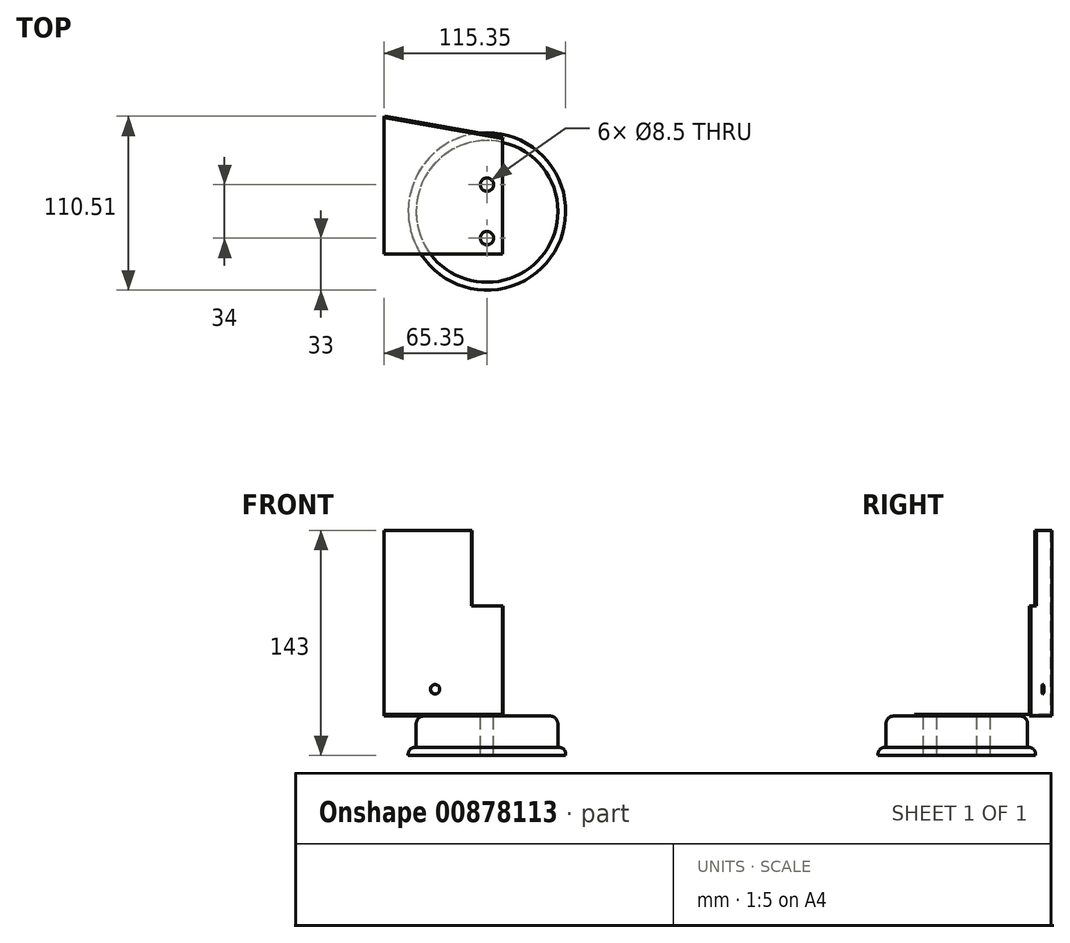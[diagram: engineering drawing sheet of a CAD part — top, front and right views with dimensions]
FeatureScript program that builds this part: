
annotation { "Feature Type Name" : "Feature", "Feature Type Description" : "" }
export const myFeature = defineFeature(function(context is Context, id is Id, definition is map)
    precondition{}
    {
        {
            var Q0;
            Q0=qCreatedBy(makeId("Top.planeOp"),FACE);
            var sketch = newSketch(context, id + "F0", { "sketchPlane" : qUnion([Q0])});
            skCircle(sketch, "E0", {"center": v(0, 0) * mm, "radius": 45 * mm});
            skLineSegment(sketch, "E1", {"start": v(0, 0) * mm, "end": v(0, 17) * mm, "construction": true});
            skLineSegment(sketch, "E2", {"start": v(0, 0) * mm, "end": v(0, -17) * mm, "construction": true});
            skCircle(sketch, "E3", {"center": v(0, 17) * mm, "radius": 4.25 * mm});
            skCircle(sketch, "E4", {"center": v(0, -17) * mm, "radius": 4.25 * mm});
            skLineSegment(sketch, "E5", {"start": v(0, -8.5) * mm, "end": v(10, -8.5) * mm, "construction": true});
            skLineSegment(sketch, "E6", {"start": v(0, -17) * mm, "end": v(0, -27) * mm, "construction": true});
            skLineSegment(sketch, "E7", {"start": v(0, 17) * mm, "end": v(0, 48) * mm, "construction": true});
            skLineSegment(sketch, "E8", {"start": v(0, 48) * mm, "end": v(-33, 48) * mm, "construction": true});
            skLineSegment(sketch, "E9", {"start": v(-33, 48) * mm, "end": v(-33, 73.27) * mm, "construction": true});
            skLineSegment(sketch, "E10", {"start": v(-68.94, 60.16) * mm, "end": v(-68.94, -27) * mm});
            skLineSegment(sketch, "E11", {"start": v(-68.94, -27) * mm, "end": v(10, -27) * mm});
            skLineSegment(sketch, "E12", {"start": v(10, -27) * mm, "end": v(10, 46.24) * mm});
            skLineSegment(sketch, "E13", {"start": v(10, 46.24) * mm, "end": v(-68.94, 60.16) * mm});
            skPoint(sketch, "E14", {"position": v(-33, 53.82) * mm});
            skSolve(sketch);
        }
        {
            var Q0;
            Q0=makeQuery(id+"F0.imprint","IMPRINT",FACE,{"disambiguationData":[TD([[makeQuery(id+"F0.imprint","IMPRINT",EDGE,{"derivedFrom":sQuery(id+"F0.wireOp",EDGE,"E0")}),1.0]])]});
            var Q1;
            Q1=makeQuery(id+"F0.imprint","IMPRINT",FACE,{"disambiguationData":[TD([[makeQuery(id+"F0.imprint","IMPRINT",EDGE,{"derivedFrom":sQuery(id+"F0.wireOp",EDGE,"E3")}),-1.0]])]});
            extrude(context, id + "F1", {"entities" : qUnion([Q0, Q1]), "oppositeDirection" : true, "depth" : 20 * mm, "offsetDistance" : 25 * mm});
        }
        {
            var Q0;
            Q0=makeQuery(id+"F1.opExtrude","CAP_EDGE",EDGE,{"disambiguationData":[OSD([sQuery(id+"F0.wireOp",EDGE,"E0")])],"isStart":true});
            fillet(context, id + "F2", {"entities" : qUnion([Q0]), "radius" : 5 * mm, "tangentPropagation" : true, "allowEdgeOverflow" : false});
        }
        {
            var Q0;
            Q0=makeQuery(id+"F1.opExtrude","CAP_FACE",FACE,{"disambiguationData":[OSD([sQuery(id+"F0.wireOp",EDGE,"E0")])],"isStart":false});
            var sketch = newSketch(context, id + "F3", { "sketchPlane" : qUnion([Q0])});
            skCircle(sketch, "E15", {"center": v(0, 0) * mm, "radius": 50 * mm});
            skSolve(sketch);
        }
        {
            var Q0;
            Q0=makeQuery(id+"F3.imprint","IMPRINT",FACE,{"disambiguationData":[TD([[makeQuery(id+"F3.imprint","IMPRINT",EDGE,{"derivedFrom":sQuery(id+"F3.wireOp",EDGE,"E15")}),1.0]])]});
            var Q1;
            Q1=makeQuery(id+"F3.imprint","IMPRINT",FACE,{"disambiguationData":[TD([[makeQuery(id+"F3.imprint","IMPRINT",EDGE,{"derivedFrom":makeQuery(id+"F1.opExtrude","CAP_EDGE",EDGE,{"disambiguationData":[OSD([sQuery(id+"F0.wireOp",EDGE,"E0")])],"isStart":false})}),-1.0]])]});
            extrude(context, id + "F4", {"entities" : qUnion([Q0, Q1]), "depth" : 5 * mm, "offsetDistance" : 25 * mm});
        }
        {
            var Q0;
            Q0=makeQuery(id+"F4.opExtrude","CAP_EDGE",EDGE,{"disambiguationData":[OSD([sQuery(id+"F3.wireOp",EDGE,"E15")])],"isStart":true});
            fillet(context, id + "F5", {"entities" : qUnion([Q0]), "radius" : 4 * mm, "tangentPropagation" : true, "allowEdgeOverflow" : false});
        }
        {
            var Q0;
            Q0=makeQuery(id+"F1.opExtrude","CAP_FACE",FACE,{"disambiguationData":[OSD([sQuery(id+"F0.wireOp",EDGE,"E0"),sQuery(id+"F0.wireOp",EDGE,"E11"),sQuery(id+"F0.wireOp",EDGE,"E12")])],"isStart":true});
            var sketch = newSketch(context, id + "F6", { "sketchPlane" : qUnion([Q0])});
            skLineSegment(sketch, "E16", {"start": v(0, 0) * mm, "end": v(0, 17) * mm, "construction": true});
            skLineSegment(sketch, "E17", {"start": v(0, 0) * mm, "end": v(0, -17) * mm, "construction": true});
            skCircle(sketch, "E18", {"center": v(0, 17) * mm, "radius": 4.25 * mm});
            skCircle(sketch, "E19", {"center": v(0, -17) * mm, "radius": 4.25 * mm});
            skLineSegment(sketch, "E20", {"start": v(0, 17) * mm, "end": v(0, 48) * mm, "construction": true});
            skLineSegment(sketch, "E21", {"start": v(0, 48) * mm, "end": v(-33, 48) * mm, "construction": true});
            skLineSegment(sketch, "E22", {"start": v(-33, 48) * mm, "end": v(-33, 83.41) * mm, "construction": true});
            skLineSegment(sketch, "E23", {"start": v(-65.35, 59.52) * mm, "end": v(-65.35, -27) * mm});
            skLineSegment(sketch, "E24", {"start": v(-65.35, -27) * mm, "end": v(10, -27) * mm});
            skLineSegment(sketch, "E25", {"start": v(10, -27) * mm, "end": v(10, 46.24) * mm});
            skLineSegment(sketch, "E26", {"start": v(10, 46.24) * mm, "end": v(-65.35, 59.52) * mm});
            skLineSegment(sketch, "E27", {"start": v(10, -17) * mm, "end": v(0, -17) * mm, "construction": true});
            skLineSegment(sketch, "E28", {"start": v(0, -17) * mm, "end": v(0, -27) * mm, "construction": true});
            skSolve(sketch);
        }
        {
            var Q0;
            {var subQ6=sQuery(id+"F6.wireOp",EDGE,"E23");Q0=makeQuery(id+"F6.imprint","IMPRINT",FACE,{"disambiguationData":[TD([[makeQuery(id+"F6.imprint","IMPRINT",EDGE,{"derivedFrom":subQ6}),1.0]])]});}
            var Q1;
            Q1=makeQuery(id+"F6.imprint","IMPRINT",FACE,{"disambiguationData":[TD([[makeQuery(id+"F6.imprint","IMPRINT",EDGE,{"derivedFrom":sQuery(id+"F6.wireOp",EDGE,"E18")}),-1.0]])]});
            extrude(context, id + "F7", {"entities" : qUnion([Q0, Q1]), "depth" : 1 * mm, "offsetDistance" : 25 * mm});
        }
        {
            var Q0;
            Q0=makeQuery(id+"F7.opExtrude","SWEPT_FACE",FACE,{"disambiguationData":[OSD([sQuery(id+"F6.wireOp",EDGE,"E26")])]});
            var sketch = newSketch(context, id + "F8", { "sketchPlane" : qUnion([Q0])});
            skLineSegment(sketch, "E29.bottom", {"start": v(-1.82, 0) * mm, "end": v(74.7, 0) * mm});
            skLineSegment(sketch, "E29.right", {"start": v(74.7, 0) * mm, "end": v(74.7, 118) * mm});
            skPoint(sketch, "E30", {"position": v(41.84, 0) * mm});
            skLineSegment(sketch, "E31", {"start": v(41.84, 0) * mm, "end": v(41.84, 17) * mm, "construction": true});
            skCircle(sketch, "E32", {"center": v(41.84, 17) * mm, "radius": 3 * mm});
            skLineSegment(sketch, "E33", {"start": v(18.18, 0) * mm, "end": v(18.18, 70) * mm, "construction": true});
            skLineSegment(sketch, "E34", {"start": v(18.18, 70) * mm, "end": v(-1.82, 70) * mm, "construction": true});
            skLineSegment(sketch, "E35", {"start": v(18.18, 70) * mm, "end": v(18.18, 118) * mm});
            skLineSegment(sketch, "E36", {"start": v(18.18, 118) * mm, "end": v(74.7, 118) * mm});
            skLineSegment(sketch, "E37", {"start": v(18.18, 70) * mm, "end": v(-1.82, 70) * mm});
            skLineSegment(sketch, "E38", {"start": v(-1.82, 70) * mm, "end": v(-1.82, 0) * mm});
            skSolve(sketch);
        }
        {
            var Q0;
            {var subQ0=sQuery(id+"F8.wireOp",EDGE,"E29.bottom");Q0=makeQuery(id+"F8.imprint","IMPRINT",FACE,{"disambiguationData":[TD([[makeQuery(id+"F8.imprint","IMPRINT",EDGE,{"derivedFrom":subQ0}),1.0]])]});}
            var Q1;
            {var subQ2=sQuery(id+"F8.wireOp",EDGE,"E29.top");Q1=makeQuery(id+"F8.imprint","IMPRINT",FACE,{"disambiguationData":[TD([[makeQuery(id+"F8.imprint","IMPRINT",EDGE,{"derivedFrom":subQ2}),-1.0]])]});}
            var Q2;
            Q2=makeQuery(id+"F8.imprint","IMPRINT",FACE,{"disambiguationData":[TD([[makeQuery(id+"F8.imprint","IMPRINT",EDGE,{"derivedFrom":sQuery(id+"F8.wireOp",EDGE,"E32")}),-1.0]])]});
            var Q3;
            {var subQ0=sQuery(id+"F8.wireOp",EDGE,"E29.bottom");Q3=makeQuery(id+"F8.imprint","IMPRINT",FACE,{"disambiguationData":[TD([[makeQuery(id+"F8.imprint","IMPRINT",EDGE,{"derivedFrom":subQ0}),1.0]])]});}
            extrude(context, id + "F9", {"entities" : qUnion([Q0, Q1, Q2, Q3]), "operationType" : NewBodyOperationType.ADD, "depth" : 1 * mm, "offsetDistance" : 25 * mm});
        }
    });
